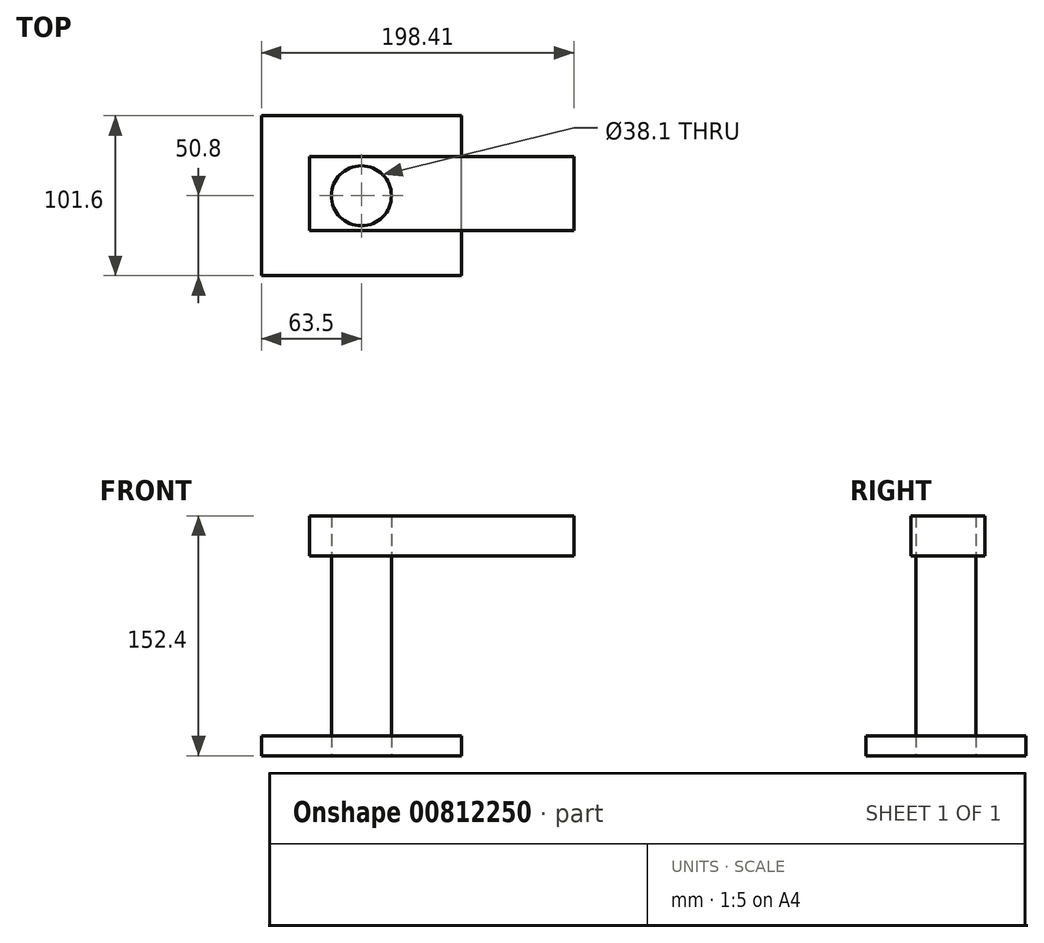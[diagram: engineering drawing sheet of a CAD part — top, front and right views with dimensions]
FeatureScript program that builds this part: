
annotation { "Feature Type Name" : "Feature", "Feature Type Description" : "" }
export const myFeature = defineFeature(function(context is Context, id is Id, definition is map)
    precondition{}
    {
        {
            var Q0;
            Q0=qCreatedBy(makeId("Top.planeOp"),FACE);
            var sketch = newSketch(context, id + "F0", { "sketchPlane" : qUnion([Q0])});
            skLineSegment(sketch, "E0.bottom", {"start": v(63.5, -50.8) * mm, "end": v(-63.5, -50.8) * mm});
            skLineSegment(sketch, "E0.top", {"start": v(63.5, 50.8) * mm, "end": v(-63.5, 50.8) * mm});
            skLineSegment(sketch, "E0.left", {"start": v(63.5, -50.8) * mm, "end": v(63.5, 50.8) * mm});
            skLineSegment(sketch, "E0.right", {"start": v(-63.5, -50.8) * mm, "end": v(-63.5, 50.8) * mm});
            skPoint(sketch, "E0.middle", {"position": v(0, 0) * mm});
            skSolve(sketch);
        }
        {
            var Q0;
            Q0=makeQuery(id+"F0.imprint","IMPRINT",FACE,{"disambiguationData":[TD([[makeQuery(id+"F0.imprint","IMPRINT",EDGE,{"derivedFrom":sQuery(id+"F0.wireOp",EDGE,"E0.bottom")}),-1.0]])]});
            extrude(context, id + "F1", {"entities" : qUnion([Q0]), "depth" : 12.7 * mm, "offsetDistance" : 25.4 * mm});
        }
        {
            var Q0;
            Q0=qCreatedBy(makeId("Top.planeOp"),FACE);
            var sketch = newSketch(context, id + "F2", { "sketchPlane" : qUnion([Q0])});
            skCircle(sketch, "E1", {"center": v(0, 0) * mm, "radius": 19.05 * mm});
            skSolve(sketch);
        }
        {
            var Q0;
            Q0 = qSketchRegion(id + "F2", true);
            extrude(context, id + "F3", {"entities" : qUnion([Q0]), "depth" : 127 * mm, "offsetDistance" : 25.4 * mm});
        }
        {
            var Q0;
            Q0=makeQuery(id+"F3.opExtrude","CAP_FACE",FACE,{"disambiguationData":[OSD([sQuery(id+"F2.wireOp",EDGE,"E1")])],"isStart":false});
            var sketch = newSketch(context, id + "F4", { "sketchPlane" : qUnion([Q0])});
            skLineSegment(sketch, "E2.bottom", {"start": v(-33.12, 24.81) * mm, "end": v(134.91, 24.81) * mm});
            skLineSegment(sketch, "E2.top", {"start": v(-33.12, -22.08) * mm, "end": v(134.91, -22.08) * mm});
            skLineSegment(sketch, "E2.left", {"start": v(-33.12, 24.81) * mm, "end": v(-33.12, -22.08) * mm});
            skLineSegment(sketch, "E2.right", {"start": v(134.91, 24.81) * mm, "end": v(134.91, -22.08) * mm});
            skSolve(sketch);
        }
        {
            var Q0;
            Q0=makeQuery(id+"F4.imprint","IMPRINT",FACE,{"disambiguationData":[TD([[makeQuery(id+"F4.imprint","IMPRINT",EDGE,{"derivedFrom":sQuery(id+"F4.wireOp",EDGE,"E2.bottom")}),-1.0]])]});
            extrude(context, id + "F5", {"entities" : qUnion([Q0]), "depth" : 25.4 * mm, "offsetDistance" : 25.4 * mm});
        }
    });
